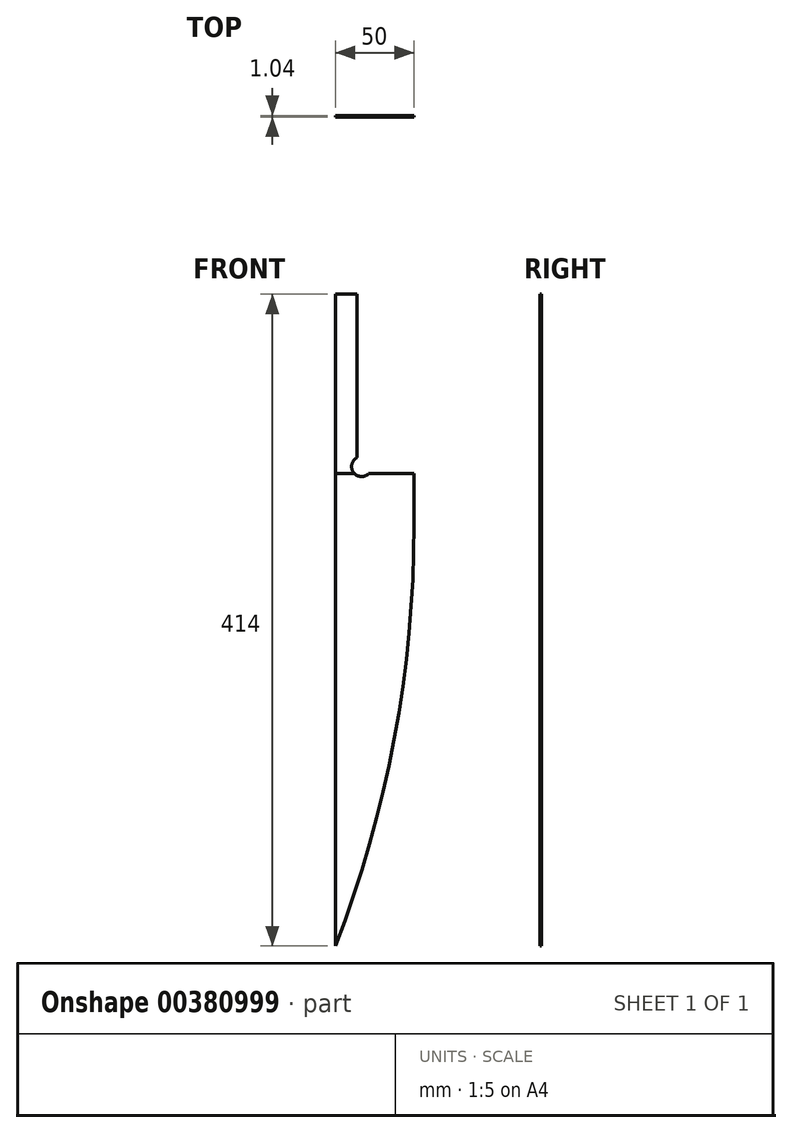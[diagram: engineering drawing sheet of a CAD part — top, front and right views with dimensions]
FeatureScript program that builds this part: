
annotation { "Feature Type Name" : "Feature", "Feature Type Description" : "" }
export const myFeature = defineFeature(function(context is Context, id is Id, definition is map)
    precondition{}
    {
        {
            var Q0;
            Q0=qCreatedBy(makeId("Top.planeOp"),FACE);
            var sketch = newSketch(context, id + "F0", { "sketchPlane" : qUnion([Q0])});
            skLineSegment(sketch, "E0.bottom", {"start": v(-25, 0.44) * mm, "end": v(25, 0.44) * mm});
            skLineSegment(sketch, "E0.top", {"start": v(-25, -0.44) * mm, "end": v(25, -0.44) * mm});
            skLineSegment(sketch, "E0.left", {"start": v(-25, 0.44) * mm, "end": v(-25, -0.44) * mm});
            skLineSegment(sketch, "E0.right", {"start": v(25, 0.44) * mm, "end": v(25, -0.44) * mm});
            skPoint(sketch, "E0.middle", {"position": v(0, 0) * mm});
            skSolve(sketch);
        }
        {
            var Q0;
            Q0=makeQuery(id+"F0.imprint","IMPRINT",FACE,{"disambiguationData":[TD([[makeQuery(id+"F0.imprint","IMPRINT",EDGE,{"derivedFrom":sQuery(id+"F0.wireOp",EDGE,"E0.bottom")}),-1.0]])]});
            extrude(context, id + "F1", {"entities" : qUnion([Q0]), "oppositeDirection" : true, "depth" : 300 * mm});
        }
        {
            var Q0;
            Q0=makeQuery(id+"F1.opExtrude","CAP_EDGE",EDGE,{"disambiguationData":[OSD([sQuery(id+"F0.wireOp",EDGE,"E0.right")])],"isStart":false});
            fillet(context, id + "F2", {"entities" : qUnion([Q0]), "radius" : 738.75 * mm, "tangentPropagation" : true, "allowEdgeOverflow" : false});
        }
        {
            var Q0;
            Q0=qCreatedBy(makeId("Top.planeOp"),FACE);
            var sketch = newSketch(context, id + "F3", { "sketchPlane" : qUnion([Q0])});
            skLineSegment(sketch, "E1.bottom", {"start": v(-25, 0.52) * mm, "end": v(-11.4, 0.52) * mm});
            skLineSegment(sketch, "E1.top", {"start": v(-25, -0.52) * mm, "end": v(-11.4, -0.52) * mm});
            skLineSegment(sketch, "E1.left", {"start": v(-25, 0.52) * mm, "end": v(-25, -0.52) * mm});
            skLineSegment(sketch, "E1.right", {"start": v(-11.4, 0.52) * mm, "end": v(-11.4, -0.52) * mm});
            skSolve(sketch);
        }
        {
            var Q0;
            Q0 = qSketchRegion(id + "F3", true);
            extrude(context, id + "F4", {"entities" : qUnion([Q0]), "operationType" : NewBodyOperationType.ADD, "depth" : 114 * mm});
        }
        {
            var Q0;
            Q0=qCreatedBy(makeId("Front.planeOp"),FACE);
            var sketch = newSketch(context, id + "F5", { "sketchPlane" : qUnion([Q0])});
            skCircle(sketch, "E2", {"center": v(-8.28, 4.6) * mm, "radius": 6.38 * mm});
            skSolve(sketch);
        }
        {
            var Q0;
            Q0=makeQuery(id+"F5.imprint","IMPRINT",FACE,{"disambiguationData":[TD([[makeQuery(id+"F5.imprint","IMPRINT",EDGE,{"derivedFrom":sQuery(id+"F5.wireOp",EDGE,"E2")}),1.0]])]});
            extrude(context, id + "F6", {"entities" : qUnion([Q0]), "operationType" : NewBodyOperationType.REMOVE, "endBound" : BoundingType.THROUGH_ALL, "oppositeDirection" : true, "depth" : 25 * mm});
        }
        {
            var Q0;
            Q0=makeQuery(id+"F6.boolean.opBoolean","COPY",FACE,{"derivedFrom":makeQuery(id+"F6.opExtrude","CAP_FACE",FACE,{"disambiguationData":[OSD([sQuery(id+"F5.wireOp",EDGE,"E2")])],"isStart":true})});
            extrude(context, id + "F7", {"entities" : qUnion([Q0]), "operationType" : NewBodyOperationType.REMOVE, "endBound" : BoundingType.THROUGH_ALL, "oppositeDirection" : true, "depth" : 25 * mm});
        }
    });
